# Revit family: Furniture_Other_Sjobergs_Workbench_Elite_2000
name_source: partatom
category: Furniture
revit_build: Autodesk Revit 2017 (Build: 20160225_1515(x64)
units: mm (PartAtom-declared; Revit-internal decimal feet)

## family parameters
Always vertical = Yes
Cut with Voids When Loaded = No
OmniClass Number = 23.40.70.14
OmniClass Title = Retail and Commercial Equipment and Furnishings
Room Calculation Point = No
Shared = No
Work Plane-Based = No

## types (2) — shared parameters
AssetType = Movable
BIMObjectName = Furniture_Other_Sjobergs_Workbench_Elite_2000
Brand = Sjöbergs
Category = Hobby
Collection = Elite
Color = Wooden
DurationUnit = Year
Features = The bench consists of cabinets and drawers SM04. 4-pack steel hooks are included.
Finish = Countertop in solid beech with double notch rows. Treated with oil.
IfcExportAs = IfcFurnishingElementType
IfcExportType = TABLE
MainColor = Wooden
Manufacturer = Sjöbergs
ManufacturerName = Sjöbergs
ManufacturerURL = https://www.sjobergs.se
Material = Wood, metal
NBSDescription = School art, design and technology tables and workbenches;
NBSReference = 45-35-20/320
Name = Sjobergs_Workbench_Elite_2000
NominalDepth = 741 mm
NominalHeight = 901 mm
ProductDatasheet = https://www.sjobergs.se
Shape = Sculptured
TableMainMaterial = Beech
TableSecondaryMaterial = Black Metal
URL = https://www.sjobergs.se
Uniclass2 = Pr_40_50_21
Uniclass2015Description = Desks, Tables And Worktops
Uniclass2015Reference = Pr_40_50_21_76
Version = 1
VersionDate = 26/06/2020
WarrantyDurationUnit = Year
zero-valued in all types: Cost

## per-type parameters (varying)
| type | Constituents | ConvergoRefNr | Description | EANNumber | ModelReference | ModelType | NominalLength | ProductInformation | Size | Weight |
| 35003 Workbench Elite 2000 + SM04 Cabinet | Elite 2000 (article n. 33458) + SM03 (article n. 33465) | 0184-2005-0016-SE | Sjöbergs Elite is both heavier and smarter than any other bench on the market. Designed and manufactured for professionals by professionals. | 7316703458202 + 7316703464043 | 35003 | 35003 Elite 2000 | 1945 mm  [stored 6.38123 ft] | Sjöbergs Elite is both heavier and smarter than any other bench on the market. Designed and manufactured for professionals by professionals. | 1945x740x900 mm | 162.0 kg |
| 35005 Workbench Elite 2000 + SM04 Cabinet + Elite clamp platform | Elite 2000 + Clamping platform (article n. 35024) + SM04 (article n. 33464) | 0184-2005-0017-SE | Together with our new Clamping Platform, our Elite benches are both more flexible and have a larger workspace. All the 19 mm large holes in the platform make the bench more useful for several tools available on the market. Also fits our tensioner ST11. You can span both from the top of the disc and the edges around the entire disc.The bench combination, which is about 2500 mm long, is made of European book and treated with first class oil. Bench hooks included. | 7316705024108 + 7316703464043 | 35005 | 35005 Elite 2000 | 2425 mm  [stored 7.95604 ft] | Together with our new Clamping Platform, our Elite benches are both more flexible and have a larger workspace. All the 19 mm large holes in the platform make the bench more useful for several tools available on the market. Also fits our tensioner ST11. You can span both from the top of the disc and the edges around the entire disc.The bench combination, which is about 2500 mm long, is made of European book and treated with first class oil. Bench hooks included. | 2425x740x900 mm | 177.0 kg |

note: column(s) folded — value = type name in every type: Model

note: [stored X ft] marks values corroborated as IEEE doubles in the binary element streams (Revit-internal decimal feet)

## geometry (parser evidence)
native form markers: Sweep x14
no freeform markers — native parametric forms only
